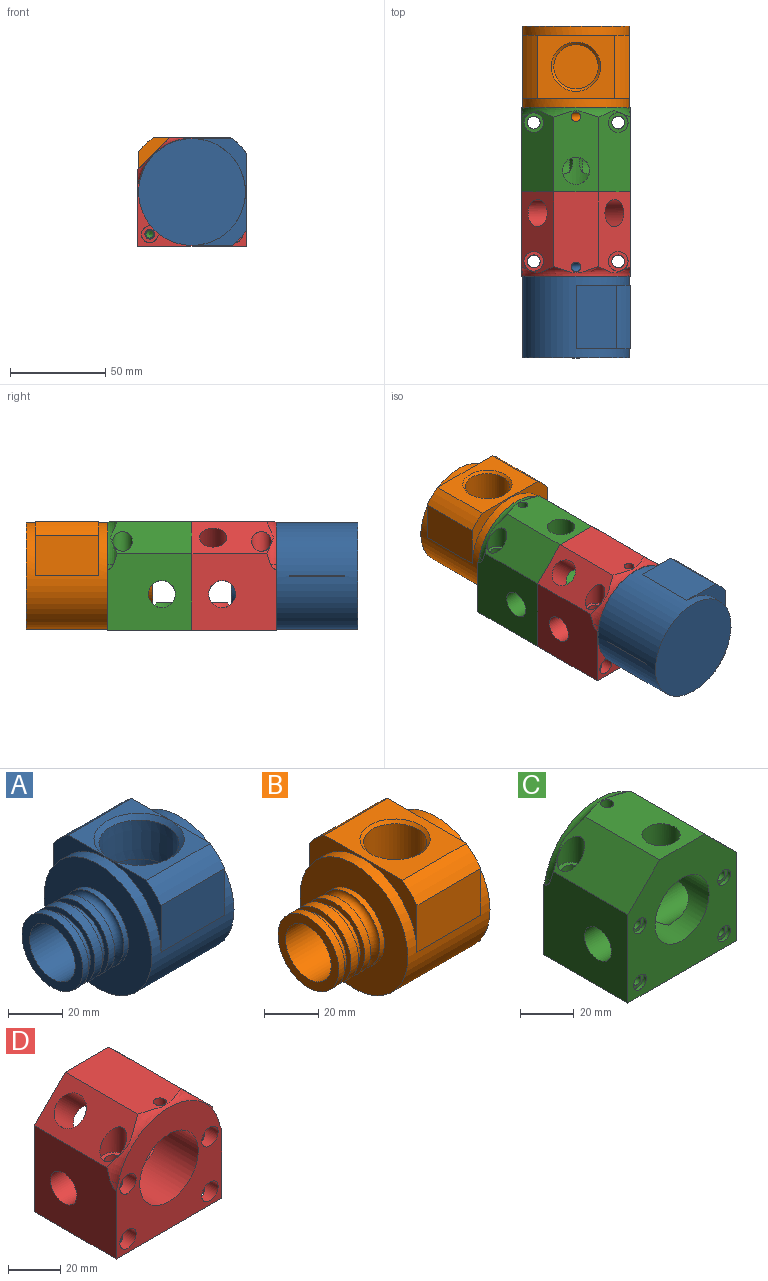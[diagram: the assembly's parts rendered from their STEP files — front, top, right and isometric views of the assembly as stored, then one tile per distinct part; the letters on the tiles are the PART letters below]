
ASSEMBLY  parts=4 mates=3
PART A: 28 faces, bbox 66.7x56.2x56.7 mm
  f0: cylinder r=14.29mm len=28.58mm, axis (0,0,-1), area 1674.9mm2, adj f1,f14,f18
  f1: cylinder r=11.91mm len=37.35mm, axis (1,0,0), area 2591.1mm2, adj f0,f6,f14
  f2: plane 31.75x31.75mm, normal (-1,0,0), area 218.1mm2, adj f5,f11
  f3: cylinder r=15.88mm len=31.75mm, axis (-1,0,0), area 316.7mm2, adj f4,f6
  f4: plane 31.75x31.75mm, normal (1,0,0), area 218.1mm2, adj f3,f5
  f5: cylinder r=13.51mm len=27.03mm, axis (1,0,0), area 269.6mm2, adj f2,f4
  f6: plane 31.75x31.75mm, normal (-1,0,0), area 346.4mm2, adj f1,f3
  f7: cylinder r=15.88mm len=31.75mm, axis (-1,0,0), area 316.7mm2, adj f10,f23
  f8: cylinder r=13.51mm len=27.03mm, axis (1,0,0), area 269.6mm2, adj f9,f10
  f9: plane 31.75x31.75mm, normal (1,0,0), area 218.1mm2, adj f8,f11
  f10: plane 31.75x31.75mm, normal (-1,0,0), area 218.1mm2, adj f7,f8
  f11: cylinder r=15.88mm len=31.75mm, axis (-1,0,0), area 395.9mm2, adj f2,f9
  f12: plane 56.2x56.2mm, normal (-1,0,0), area 1688.7mm2, adj f21,f22
  f13: cone r=14.83mm half-angle=45.9deg, axis (0,0,1), area 252.6mm2, adj f14,f15
  f14: cone r=14.29mm half-angle=1.8deg, axis (0,0,1), area 1577.2mm2, adj f0,f1,f13
  f15: plane 40.85x33.34mm, normal (0,0,1), area 489.8mm2, adj f13,f19,f20,f26,f27
  f16: plane 29.11x0.02mm, normal (0,0,-1), area 0.6mm2, adj f21
  f17: plane 56.2x56.2mm, normal (1,0,0), area 2480.4mm2, adj f21
  f18: plane 28.58x28.58mm, normal (0,0,1), area 641.3mm2, adj f0
  f19: cylinder r=35.12mm len=33.34mm, axis (-1,0,0), area 359.2mm2, adj f15,f24,f26,f27
  f20: cylinder r=35.12mm len=33.34mm, axis (-1,0,0), area 359.2mm2, adj f15,f25,f26,f27
  f21: cylinder r=28.1mm len=56.2mm, axis (-1,0,0), area 4623.9mm2, adj f12,f16,f17,f24,f25,f26,f27
  f22: cylinder r=15.88mm len=31.75mm, axis (-1,0,0), area 237.5mm2, adj f12,f23
  f23: torus R=15.88mm, axis (-1,0,0), area 674.9mm2, adj f7,f22
  f24: plane 33.34x21.07mm, normal (0,-1,0), area 702.6mm2, adj f19,f21,f26,f27
  f25: plane 33.34x21.07mm, normal (0,1,0), area 702.6mm2, adj f20,f21,f26,f27
  f26: plane 56.2x28.58mm, normal (-1,0,0), area 314mm2, adj f15,f19,f20,f21,f24,f25
  f27: plane 56.2x28.58mm, normal (1,0,0), area 314mm2, adj f15,f19,f20,f21,f24,f25
PART B: 33 faces, bbox 66.7x56.2x56.7 mm
  f0: cylinder r=16.67mm len=23.82mm, axis (0,0,-1), area 17.4mm2, adj f1,f10
  f1: cylinder r=11.71mm len=23.42mm, axis (1,0,0), area 544.7mm2, adj f0,f2,f3,f6
  f2: plane 4.13x0.18mm, normal (-1,0,0), area 0.5mm2, adj f1,f6
  f3: plane 4.13x0.18mm, normal (-1,0,0), area 0.5mm2, adj f1,f6
  f4: cylinder r=14.29mm len=28.58mm, axis (0,0,-1), area 199.5mm2, adj f5,f7
  f5: plane 28.58x28.58mm, normal (0,0,1), area 641.3mm2, adj f4
  f6: cylinder r=11.71mm len=39.37mm, axis (0,0,-1), area 2402mm2, adj f1,f2,f3,f7,f32
  f7: plane 28.58x28.58mm, normal (0,0,-1), area 210.6mm2, adj f4,f6
  f8: torus R=15.88mm, axis (-1,0,0), area 674.9mm2, adj f9,f26
  f9: cylinder r=15.88mm len=31.75mm, axis (-1,0,0), area 237.5mm2, adj f8,f21
  f10: cylinder r=11.91mm len=28.58mm, axis (1,0,0), area 2137.7mm2, adj f0,f27
  f11: plane 33.34x21.07mm, normal (0,-1,0), area 702.6mm2, adj f13,f14,f15,f17
  f12: plane 33.34x21.07mm, normal (0,1,0), area 702.6mm2, adj f13,f14,f15,f16
  f13: plane 56.2x28.58mm, normal (-1,0,0), area 314mm2, adj f11,f12,f14,f16,f17,f20
  f14: cylinder r=28.1mm len=56.2mm, axis (-1,0,0), area 4623.9mm2, adj f11,f12,f13,f15,f18,f19,f21
  f15: plane 56.2x28.58mm, normal (1,0,0), area 314mm2, adj f11,f12,f14,f16,f17,f20
  f16: cylinder r=35.12mm len=33.34mm, axis (-1,0,0), area 359.2mm2, adj f12,f13,f15,f20
  f17: cylinder r=35.12mm len=33.34mm, axis (-1,0,0), area 359.2mm2, adj f11,f13,f15,f20
  f18: plane 56.2x56.2mm, normal (1,0,0), area 2480.4mm2, adj f14
  f19: plane 29.11x0.02mm, normal (0,0,-1), area 0.6mm2, adj f14
  f20: plane 40.85x33.34mm, normal (0,0,1), area 832.5mm2, adj f13,f15,f16,f17,f32
  f21: plane 56.2x56.2mm, normal (-1,0,0), area 1688.7mm2, adj f9,f14
  f22: cylinder r=15.88mm len=31.75mm, axis (-1,0,0), area 395.9mm2, adj f24,f28
  f23: plane 31.75x31.75mm, normal (-1,0,0), area 218.1mm2, adj f25,f26
  f24: plane 31.75x31.75mm, normal (1,0,0), area 218.1mm2, adj f22,f25
  f25: cylinder r=13.51mm len=27.03mm, axis (1,0,0), area 269.6mm2, adj f23,f24
  f26: cylinder r=15.88mm len=31.75mm, axis (-1,0,0), area 316.7mm2, adj f8,f23
  f27: plane 31.75x31.75mm, normal (-1,0,0), area 346.4mm2, adj f10,f31
  f28: plane 31.75x31.75mm, normal (-1,0,0), area 218.1mm2, adj f22,f29
  f29: cylinder r=13.51mm len=27.03mm, axis (1,0,0), area 269.6mm2, adj f28,f30
  f30: plane 31.75x31.75mm, normal (1,0,0), area 218.1mm2, adj f29,f31
  f31: cylinder r=15.88mm len=31.75mm, axis (-1,0,0), area 316.7mm2, adj f27,f30
  f32: cone r=11.71mm half-angle=45deg, axis (0,0,1), area 139.3mm2, adj f6,f20
PART C: 43 faces, bbox 75.4x46.6x68.3 mm
  f0: cylinder r=15.88mm len=31.75mm, axis (0,1,0), area 2380.4mm2, adj f1,f2,f11,f12,f13,f14,f15,f17
  f1: cone r=0mm half-angle=59deg, axis (0,1,0), area 9.7mm2, adj f0,f3,f13,f14
  f2: cone r=0mm half-angle=59deg, axis (0,1,0), area 99.6mm2, adj f0,f3,f12,f15
  f3: cylinder r=14.29mm len=28.58mm, axis (0,-1,0), area 1189.8mm2, adj f1,f2,f10,f12,f13,f14,f15,f16
  f4: plane 45.68x41.64mm, normal (-1,0,0), area 1606.1mm2, adj f5,f9,f10,f11,f15,f35,f36
  f5: plane 57.15x44.45mm, normal (0,0,-1), area 2468.6mm2, adj f4,f6,f10,f11,f37,f41
  f6: plane 45.68x41.64mm, normal (1,0,0), area 1606.1mm2, adj f5,f7,f10,f11,f12,f34,f35
  f7: plane 44.84x18.91mm, normal (0.71,0,0.71), area 857mm2, adj f6,f8,f10,f35,f40
  f8: plane 42.68x23.69mm, normal (0,0,1), area 795.5mm2, adj f7,f9,f10,f16,f17,f35
  f9: plane 42.68x16.74mm, normal (-0.71,0,0.71), area 857mm2, adj f4,f8,f10,f35,f39
  f10: plane 57.15x57.15mm, normal (0,-1,0), area 2206.6mm2, adj f3,f4,f5,f6,f7,f8,f9,f20
  f11: plane 57.15x56.9mm, normal (0,1,0), area 2104.5mm2, adj f0,f4,f5,f6,f34,f35,f36
  f12: cylinder r=7.14mm len=25.4mm, axis (1,0,0), area 839.4mm2, adj f0,f2,f3,f6,f13
  f13: cone r=0mm half-angle=59deg, axis (1,0,0), area 19.9mm2, adj f0,f1,f3,f12
  f14: cone r=0mm half-angle=59deg, axis (-1,0,0), area 19.9mm2, adj f0,f1,f3,f15
  f15: cylinder r=7.14mm len=25.4mm, axis (-1,0,0), area 839.5mm2, adj f0,f2,f3,f4,f14
  f16: cylinder r=7.14mm len=16.2mm, axis (0,0,1), area 682.8mm2, adj f3,f8
  f17: cylinder r=2.5mm len=12.9mm, axis (0,0,1), area 200.3mm2, adj f0,f8
  f18: cylinder r=2.02mm len=16.19mm, axis (0,-1,0), area 205.4mm2, adj f19,f21
  f19: plane 6.63x6.63mm, normal (0,-1,0), area 21.7mm2, adj f18,f20
  f20: cylinder r=3.31mm len=6.63mm, axis (0,-1,0), area 33.1mm2, adj f10,f19
  f21: cone r=0mm half-angle=59deg, axis (0,-1,0), area 14.9mm2, adj f18
  f22: cylinder r=2.02mm len=16.19mm, axis (0,-1,0), area 205.4mm2, adj f23,f25
  f23: plane 6.63x6.63mm, normal (0,-1,0), area 21.7mm2, adj f22,f24
  f24: cylinder r=3.31mm len=6.63mm, axis (0,-1,0), area 33.1mm2, adj f10,f23
  f25: cone r=0mm half-angle=59deg, axis (0,-1,0), area 14.9mm2, adj f22
  f26: cylinder r=2.02mm len=16.19mm, axis (0,-1,0), area 205.4mm2, adj f27,f29
  f27: plane 6.63x6.63mm, normal (0,-1,0), area 21.7mm2, adj f26,f28
  f28: cylinder r=3.31mm len=6.63mm, axis (0,-1,0), area 33.1mm2, adj f10,f27
  f29: cone r=0mm half-angle=59deg, axis (0,-1,0), area 14.9mm2, adj f26
  f30: cylinder r=2.02mm len=16.19mm, axis (0,-1,0), area 205.4mm2, adj f31,f33
  f31: plane 6.63x6.63mm, normal (0,-1,0), area 21.7mm2, adj f30,f32
  f32: cylinder r=3.31mm len=6.63mm, axis (0,-1,0), area 33.1mm2, adj f10,f31
  f33: cone r=0mm half-angle=59deg, axis (0,-1,0), area 14.9mm2, adj f30
  f34: torus R=18.8mm, axis (0,-1,0), area 4.9mm2, adj f6,f11,f35
  f35: torus R=34.67mm, axis (0,1,0), area 281mm2, adj f4,f6,f7,f8,f9,f11,f34,f36
  f36: torus R=18.8mm, axis (0,-1,0), area 4.9mm2, adj f4,f11,f35
  f37: cylinder r=3.38mm len=39.37mm, axis (0,0,1), area 835.7mm2, adj f5,f38
  f38: plane 10.31x10.31mm, normal (0,0,1), area 47.7mm2, adj f37,f39
  f39: cylinder r=5.16mm len=12.55mm, axis (0,0,1), area 239.5mm2, adj f9,f38
  f40: cylinder r=5.16mm len=12.55mm, axis (0,0,1), area 239.5mm2, adj f7,f42
  f41: cylinder r=3.38mm len=39.37mm, axis (0,0,1), area 835.7mm2, adj f5,f42
  f42: plane 10.31x10.31mm, normal (0,0,1), area 47.7mm2, adj f40,f41
PART D: 56 faces, bbox 75.4x51.1x68.3 mm
  f0: plane 31.75x31.75mm, normal (0,1,0), area 150.4mm2, adj f12,f53
  f1: cylinder r=2.55mm len=5.11mm, axis (0,-1,0), area 50.9mm2, adj f35,f51
  f2: cylinder r=2.55mm len=5.11mm, axis (0,-1,0), area 50.9mm2, adj f38,f49
  f3: cylinder r=2.55mm len=5.11mm, axis (0,-1,0), area 50.9mm2, adj f40,f47
  f4: cylinder r=2.55mm len=5.11mm, axis (0,-1,0), area 50.9mm2, adj f42,f45
  f5: cylinder r=3.38mm len=6.76mm, axis (0,0,1), area 75.6mm2, adj f22,f43
  f6: cylinder r=3.38mm len=6.76mm, axis (0,0,1), area 57.2mm2, adj f14,f41
  f7: cylinder r=3.38mm len=6.76mm, axis (0,0,1), area 57.2mm2, adj f14,f39
  f8: cylinder r=3.38mm len=6.76mm, axis (0,0,1), area 75.6mm2, adj f23,f36
  f9: cylinder r=15.88mm len=31.75mm, axis (0,-1,0), area 2380.3mm2, adj f10,f11,f20,f28,f29,f30,f31,f32
  f10: cone r=0mm half-angle=59deg, axis (0,-1,0), area 9.7mm2, adj f9,f12,f30,f31
  f11: cone r=0mm half-angle=59deg, axis (0,-1,0), area 99.6mm2, adj f9,f12,f29,f32
  f12: cylinder r=14.29mm len=28.58mm, axis (0,1,0), area 1022.8mm2, adj f0,f10,f11,f29,f30,f31,f32,f33
  f13: plane 45.68x41.64mm, normal (-1,0,0), area 1606.1mm2, adj f14,f18,f19,f20,f25,f26,f32
  f14: plane 57.15x44.45mm, normal (0,0,-1), area 2468.6mm2, adj f6,f7,f13,f15,f19,f20
  f15: plane 45.68x41.64mm, normal (1,0,0), area 1606.1mm2, adj f14,f16,f19,f20,f25,f27,f29
  f16: plane 44.84x18.91mm, normal (0.71,0,0.71), area 696.9mm2, adj f15,f17,f19,f24,f25,f33
  f17: plane 42.68x23.69mm, normal (0,0,1), area 955.5mm2, adj f16,f18,f19,f25,f28
  f18: plane 42.68x16.74mm, normal (-0.71,0,0.71), area 696.9mm2, adj f13,f17,f19,f21,f25,f34
  f19: plane 57.15x57.15mm, normal (0,1,0), area 1722.9mm2, adj f13,f14,f15,f16,f17,f18,f46,f48
  f20: plane 57.15x56.9mm, normal (0,-1,0), area 1859mm2, adj f9,f13,f14,f15,f25,f26,f27,f36
  f21: cylinder r=5.16mm len=12.55mm, axis (0,0,1), area 239.5mm2, adj f18,f22
  f22: plane 10.31x10.31mm, normal (0,0,1), area 47.7mm2, adj f5,f21
  f23: plane 10.31x10.31mm, normal (0,0,1), area 47.7mm2, adj f8,f24
  f24: cylinder r=5.16mm len=12.55mm, axis (0,0,1), area 239.5mm2, adj f16,f23
  f25: torus R=34.67mm, axis (0,1,0), area 281mm2, adj f13,f15,f16,f17,f18,f20,f26,f27
  f26: torus R=18.8mm, axis (0,-1,0), area 4.9mm2, adj f13,f20,f25
  f27: torus R=18.8mm, axis (0,-1,0), area 4.9mm2, adj f15,f20,f25
  f28: cylinder r=2.5mm len=12.9mm, axis (0,0,1), area 202.6mm2, adj f9,f17
  f29: cylinder r=7.14mm len=25.4mm, axis (1,0,0), area 839.4mm2, adj f9,f11,f12,f15,f30
  f30: cone r=0mm half-angle=59deg, axis (1,0,0), area 19.9mm2, adj f9,f10,f12,f29
  f31: cone r=0mm half-angle=59deg, axis (-1,0,0), area 19.9mm2, adj f9,f10,f12,f32
  f32: cylinder r=7.14mm len=25.4mm, axis (-1,0,0), area 839.5mm2, adj f9,f11,f12,f13,f31
  f33: cylinder r=7.14mm len=21.55mm, axis (0.71,0,0.71), area 682.8mm2, adj f12,f16
  f34: cylinder r=7.14mm len=21.55mm, axis (-0.71,0,0.71), area 682.8mm2, adj f12,f18
  f35: plane 8.84x8.84mm, normal (0,-1,0), area 40.9mm2, adj f1,f36
  f36: cylinder r=4.42mm len=22.86mm, axis (0,-1,0), area 562.8mm2, adj f8,f20,f35,f37
  f37: cylinder r=3.38mm len=20.08mm, axis (0,0,1), area 391.6mm2, adj f36,f39
  f38: plane 8.84x8.84mm, normal (0,-1,0), area 40.9mm2, adj f2,f39
  f39: cylinder r=4.42mm len=22.86mm, axis (0,-1,0), area 562.8mm2, adj f7,f20,f37,f38
  f40: plane 8.84x8.84mm, normal (0,-1,0), area 40.9mm2, adj f3,f41
  f41: cylinder r=4.42mm len=22.86mm, axis (0,-1,0), area 562.8mm2, adj f6,f20,f40,f44
  f42: plane 8.84x8.84mm, normal (0,-1,0), area 40.9mm2, adj f4,f43
  f43: cylinder r=4.42mm len=22.86mm, axis (0,-1,0), area 562.8mm2, adj f5,f20,f42,f44
  f44: cylinder r=3.38mm len=20.08mm, axis (0,0,1), area 391.6mm2, adj f41,f43
  f45: plane 6.63x6.63mm, normal (0,1,0), area 14mm2, adj f4,f46
  f46: cylinder r=3.31mm len=18.42mm, axis (0,1,0), area 383.5mm2, adj f19,f45
  f47: plane 6.63x6.63mm, normal (0,1,0), area 14mm2, adj f3,f48
  f48: cylinder r=3.31mm len=18.42mm, axis (0,1,0), area 383.5mm2, adj f19,f47
  f49: plane 6.63x6.63mm, normal (0,1,0), area 14mm2, adj f2,f50
  f50: cylinder r=3.31mm len=18.42mm, axis (0,1,0), area 383.5mm2, adj f19,f49
  f51: plane 6.63x6.63mm, normal (0,1,0), area 14mm2, adj f1,f52
  f52: cylinder r=3.31mm len=18.42mm, axis (0,1,0), area 383.5mm2, adj f19,f51
  f53: cylinder r=15.88mm len=31.75mm, axis (0,1,0), area 202.7mm2, adj f0,f55
  f54: cylinder r=18.92mm len=37.85mm, axis (0,1,0), area 241.6mm2, adj f19,f55
  f55: plane 37.85x37.85mm, normal (0,1,0), area 333.2mm2, adj f53,f54
PLACE A rot(axis=(-0.58,0.58,-0.58),120deg) t=(0.24,-65.09,0)mm
PLACE B rot(axis=(0,0,1),90deg) t=(0,-23.81,0.24)mm
PLACE C at identity fixed
PLACE D t=(0,-88.9,0)mm
MATE revolute B.f16 <-> C.f0  axis (0,-1,0) through (0,0,0)mm
MATE fastened C.f0 <-> D.f9  axis (0,-1,0) through (0,-44.45,0)mm
MATE revolute A.f20 <-> D.f9  axis (0,1,0) through (0,-88.9,0)mm
